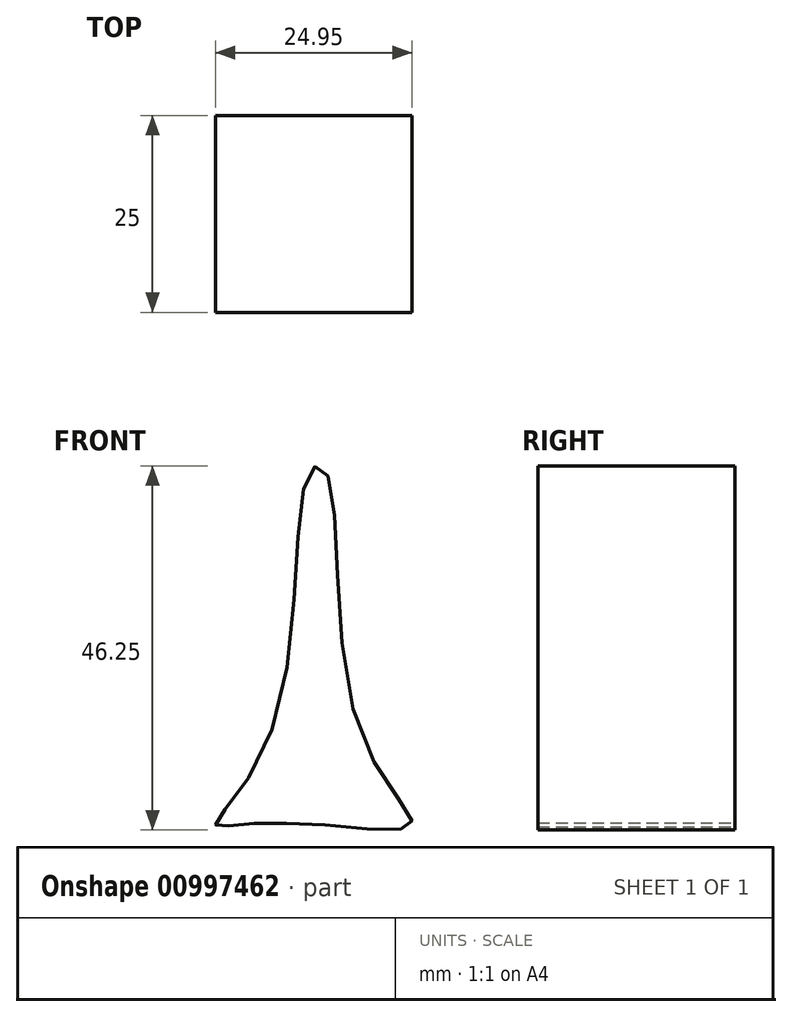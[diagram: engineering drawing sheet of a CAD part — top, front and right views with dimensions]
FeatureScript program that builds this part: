
annotation { "Feature Type Name" : "Feature", "Feature Type Description" : "" }
export const myFeature = defineFeature(function(context is Context, id is Id, definition is map)
    precondition{}
    {
        {
            var Q0;
            Q0=qCreatedBy(makeId("Front.planeOp"),FACE);
            var sketch = newSketch(context, id + "F0", { "sketchPlane" : qUnion([Q0])});
            skFitSpline(sketch, "E0", {"points": [v(0, 0) * mm, v(-11.48, 0) * mm, v(-13.9, 0) * mm, v(-6.81, 11.85) * mm, v(-1.96, 44.88) * mm, v(0, 45.07) * mm, v(4.39, 12.04) * mm, v(10.92, 0) * mm, v(0, 0) * mm]});
            skSolve(sketch);
        }
        {
            var Q0;
            Q0 = qSketchRegion(id + "F0", true);
            extrude(context, id + "F1", {"entities" : qUnion([Q0]), "depth" : 25 * mm, "offsetDistance" : 25 * mm});
        }
    });
